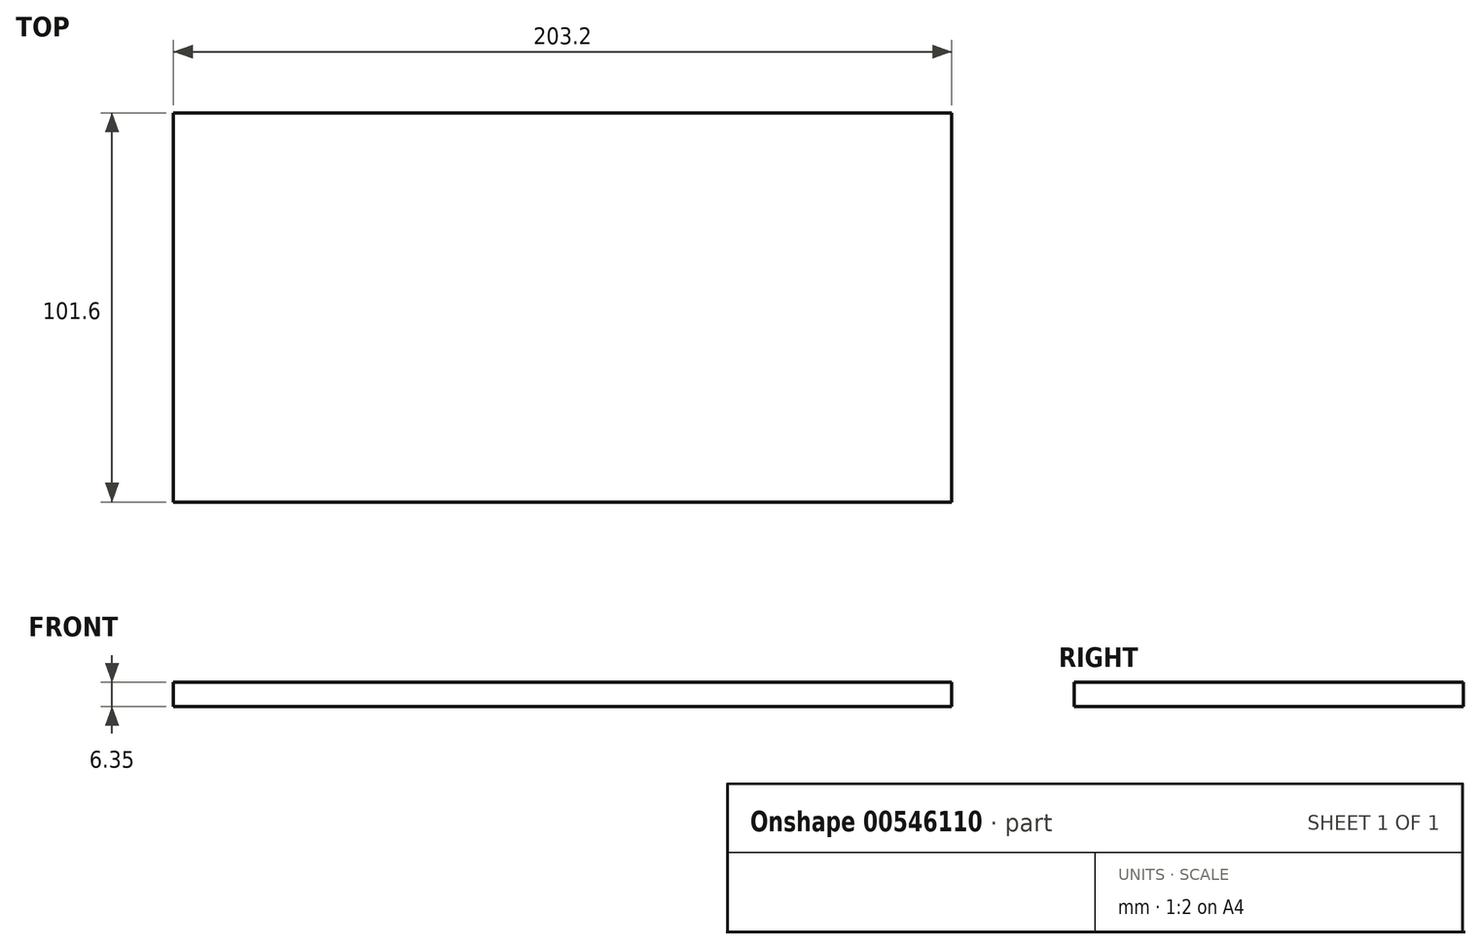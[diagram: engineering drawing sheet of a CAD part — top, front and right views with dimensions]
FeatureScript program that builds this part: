
annotation { "Feature Type Name" : "Feature", "Feature Type Description" : "" }
export const myFeature = defineFeature(function(context is Context, id is Id, definition is map)
    precondition{}
    {
        {
            var Q0;
            Q0=qCreatedBy(makeId("Front.planeOp"),FACE);
            var sketch = newSketch(context, id + "F0", { "sketchPlane" : qUnion([Q0])});
            skLineSegment(sketch, "E0.bottom", {"start": v(101.36, -58.96) * mm, "end": v(-101.84, -58.96) * mm});
            skLineSegment(sketch, "E0.top", {"start": v(101.36, -65.3) * mm, "end": v(-101.84, -65.3) * mm});
            skLineSegment(sketch, "E0.left", {"start": v(101.36, -58.96) * mm, "end": v(101.36, -65.3) * mm});
            skLineSegment(sketch, "E0.right", {"start": v(-101.84, -58.96) * mm, "end": v(-101.84, -65.3) * mm});
            skSolve(sketch);
        }
        {
            var Q0;
            Q0 = qSketchRegion(id + "F0", true);
            extrude(context, id + "F1", {"entities" : qUnion([Q0]), "endBound" : BoundingType.SYMMETRIC, "oppositeDirection" : true, "depth" : 101.6 * mm, "offsetDistance" : 25.4 * mm});
        }
    });
